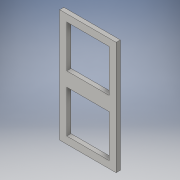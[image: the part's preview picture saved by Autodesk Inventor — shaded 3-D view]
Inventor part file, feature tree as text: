
AUTODESK INVENTOR PART (.ipt)
format: ipt  version: 2016 (Build 200138000, 138)  size: 111,616 bytes
history: native  units: mm
features: extrude x2, sketch x2
ambient origin geometry x8: Origin, YZ Plane, XZ Plane, XY Plane, X Axis, Y Axis, Z Axis, Center Point
bodies: Solid1 (feature_tree)
feature tree (4):
  extrude  "Extrusion1"  Depth=80.0mm
  extrude  "Extrusion2"  Depth=5.0mm
  sketch  "Sketch1"  dims[d0=40.0mm d1=80.0mm]
  sketch  "Sketch3"  dims[d2=3.0mm d3=0.0mm d4=5.0mm d5=30.0mm d6=10.0mm d7=30.0mm d8=5.0mm d9=5.0mm d10=3.0mm d11=0.0mm]
